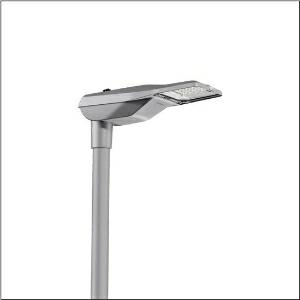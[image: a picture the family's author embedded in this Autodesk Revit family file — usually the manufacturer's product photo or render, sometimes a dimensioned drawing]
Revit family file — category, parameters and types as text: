
# Revit family: streetlight_sl_21_micro___st1_5a_5xe1p33s08db_10f0
name_source: partatom
category: Lighting Fixtures
units: mm (PartAtom-declared; Revit-internal decimal feet)

## family parameters
Cut with Voids When Loaded = No
Host = Face
Light Source = No
Part Type = Normal
Room Calculation Point = No
Round Connector Dimension = Use Diameter
Shared = No

## types (1)
- --- (1 x LED, 5020 lm, 39.1 W, 3000K)
    Apparent Load = 39 VA
    CIE Flux Codes = 22 53 95 100 100
    Color Rendering = 70
    Color Temperature = 3000K
    Default Elevation = 1800 mm
    Description = Streetlight SL 21 micro, mast luminaire, primary light control with lens, of PMMA, primary optical cover: cover, of toughened safety glass, transparent, light distribution: ST1.5a, light emission: direct distribution, primary light characteristic: asymmetric, installation type: side-entry, post-top, LED, High Power LED, rated luminous flux: 5.020lm, luminous efficacy: 128lm/W, light colour: 730, colour temperature: 3000K, control gear: D4i, control: flexible luminous flux parameterisation, time-dependent luminous flux control, constant luminous flux control, overheat protection, pre-setting: logarithmic dimming characteristic, mains connection: 220..240V, AC, 50/60Hz, start of lifetime: 39W, end of service life: 41W, reduction: 18W, luminaire housing, of diecast aluminium, powder-coated, SITECO metallic grey (DB 702S), corrosivity category C5 high according to DIN EN ISO 12944, please order mast flange separately, inclination adjustable: 0°, 5°, 10°, 15°, sealing non-destructively replaceable, multi-level sealing system, length: 528mm, width: 235mm, height: 110mm, mast flange for spigot size: 42mm (side-entry): 5XC10008XM4, 60/48mm (side-entry/post-top): 5XC10108XM2, 76/60mm (side-entry/post-top): 5XC10108XM1, Smart Interface above, protection rating (complete): IP66, insulation class (complete): insulation class II (safety insulation), certification: CE, ENEC, ENEC+, VDE, impact resistance: IK10, permissible operating ambient temperature for outdoor applications: -40..+50°C, standard-compliant lighting for roads and squares, packaging unit: 1 piece

Light Distribution: ST1.5a
    Height = 110 mm
    Lamp = 1 x LED
    Lamp Light Flux = 5020 lm
    Lamp Power = 39.1 W
    Lamp count = 1
    Length = 528 mm
    Luminous efficacy = 128 lm/W
    Manufacturer = Siteco
    ModVariant = No
    Model = 5XE1P33S08DB
    Number of Poles = 1
    OnlyDefault = Yes
    Power Factor = 1
    Product Name = Streetlight SL 21 micro | ST1.5a
    Product group = mast luminaire | pylon top
    ProductGroupID = 6100
    Protection Class = Protection class II
    Protection Degree = IP 66
    RLX_Detail_Level = 1
    RLX_Emergency_Light_Flux = 0 lm
    RLX_Emergency_Type = 0
    RLX_Emergency_Type_DB = No
    RlxData = <blob elided: 101653 chars, md5=93b732d5>
    Socket = socket
    Standby Power = 0 W
    System Light Flux = 5020 lm
    System Power = 39 W
    Type Comments = factory setting: luminous flux: 100 % | dim-lin: 254 | 765 mA
    Type Image = l_1277292.jpg
    URL = http://relux.com
    VarID = @adj_153241
    Voltage = 0 V
    Weight = 0.00 kg
    Width = 235 mm

## geometry (parser evidence)
native form markers: Blend x4, Sweep x10
no freeform markers — native parametric forms only
